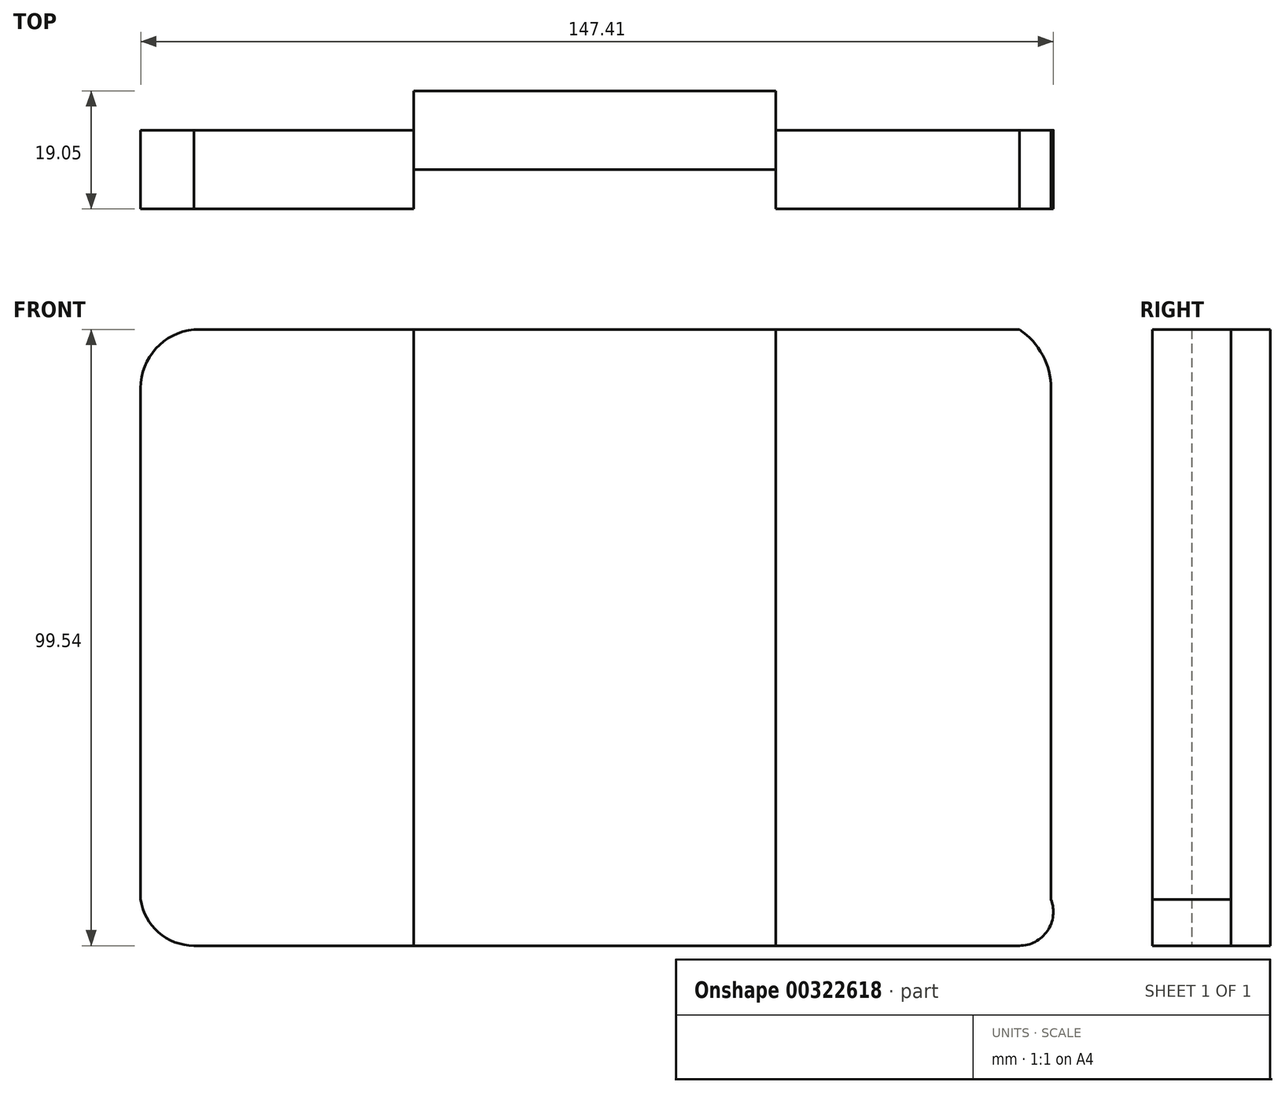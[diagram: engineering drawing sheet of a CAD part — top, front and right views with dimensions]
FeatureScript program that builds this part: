
annotation { "Feature Type Name" : "Feature", "Feature Type Description" : "" }
export const myFeature = defineFeature(function(context is Context, id is Id, definition is map)
    precondition{}
    {
        {
            var Q0;
            Q0=qCreatedBy(makeId("Front.planeOp"),FACE);
            var sketch = newSketch(context, id + "F0", { "sketchPlane" : qUnion([Q0])});
            skLineSegment(sketch, "E0", {"start": v(-62.16, 49.08) * mm, "end": v(-62.16, -33.47) * mm});
            skLineSegment(sketch, "E1", {"start": v(-53.57, 58.54) * mm, "end": v(79.78, 58.54) * mm});
            skArc(sketch, "E2", {"start": v(-53.57, 58.54) * mm, "mid": v(-59.7, 55.47) * mm, "end": v(-62.16, 49.08) * mm});
            skLineSegment(sketch, "E3", {"start": v(-53.57, -41) * mm, "end": v(79.78, -41) * mm});
            skArc(sketch, "E4", {"start": v(-62.16, -33.47) * mm, "mid": v(-59.28, -38.85) * mm, "end": v(-53.57, -41) * mm});
            skLineSegment(sketch, "E5", {"start": v(84.89, 49) * mm, "end": v(84.89, -33.55) * mm});
            skArc(sketch, "E6", {"start": v(79.78, -41) * mm, "mid": v(84.3, -38.62) * mm, "end": v(84.89, -33.55) * mm});
            skArc(sketch, "E7", {"start": v(84.89, 49) * mm, "mid": v(83.53, 54.4) * mm, "end": v(79.78, 58.54) * mm});
            skLineSegment(sketch, "E8", {"start": v(-18.09, 58.54) * mm, "end": v(-18.09, -41) * mm});
            skLineSegment(sketch, "E9", {"start": v(40.44, 58.54) * mm, "end": v(40.44, -41) * mm});
            skSolve(sketch);
        }
        {
            var Q0;
            Q0=makeQuery(id+"F0.imprint","IMPRINT",FACE,{"disambiguationData":[TD([[makeQuery(id+"F0.imprint","IMPRINT",EDGE,{"derivedFrom":sQuery(id+"F0.wireOp",EDGE,"E0")}),1.0]])]});
            var Q1;
            Q1=makeQuery(id+"F0.imprint","IMPRINT",FACE,{"disambiguationData":[TD([[makeQuery(id+"F0.imprint","IMPRINT",EDGE,{"derivedFrom":sQuery(id+"F0.wireOp",EDGE,"E5")}),-1.0]])]});
            extrude(context, id + "F1", {"entities" : qUnion([Q0, Q1]), "endBound" : BoundingType.SYMMETRIC, "depth" : 12.7 * mm});
        }
        {
            var Q0;
            {var subQ0=sQuery(id+"F0.wireOp",EDGE,"E8");Q0=makeQuery(id+"F0.imprint","IMPRINT",FACE,{"disambiguationData":[TD([[makeQuery(id+"F0.imprint","IMPRINT",EDGE,{"derivedFrom":subQ0}),1.0]])]});}
            extrude(context, id + "F2", {"entities" : qUnion([Q0]), "oppositeDirection" : true, "depth" : 12.7 * mm});
        }
    });
